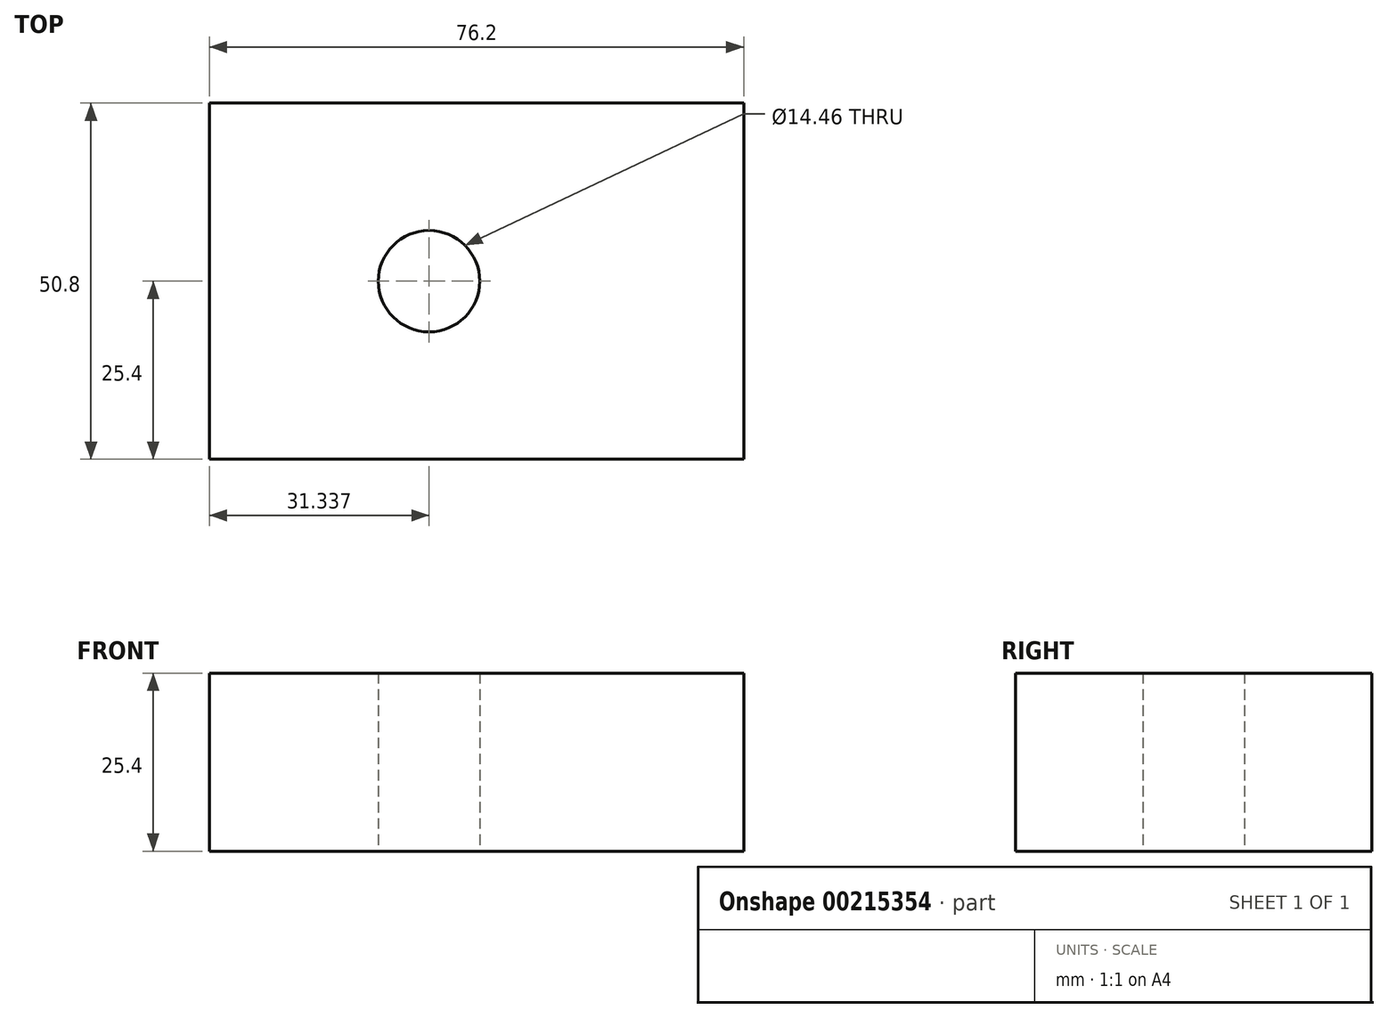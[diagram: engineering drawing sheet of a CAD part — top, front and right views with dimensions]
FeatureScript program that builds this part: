
annotation { "Feature Type Name" : "Feature", "Feature Type Description" : "" }
export const myFeature = defineFeature(function(context is Context, id is Id, definition is map)
    precondition{}
    {
        {
            var Q0;
            Q0=qCreatedBy(makeId("Top.planeOp"),FACE);
            var sketch = newSketch(context, id + "F0", { "sketchPlane" : qUnion([Q0])});
            skLineSegment(sketch, "E0", {"start": v(0, 0) * mm, "end": v(76.2, 0) * mm});
            skLineSegment(sketch, "E1", {"start": v(0, 50.8) * mm, "end": v(0, 0) * mm});
            skLineSegment(sketch, "E2", {"start": v(0, 50.8) * mm, "end": v(76.2, 50.8) * mm});
            skLineSegment(sketch, "E3", {"start": v(76.2, 50.8) * mm, "end": v(76.2, 0) * mm});
            skCircle(sketch, "E4", {"center": v(31.34, 25.4) * mm, "radius": 7.23 * mm});
            skPoint(sketch, "E4.centerSnap0", {"position": v(0, 25.4) * mm});
            skSolve(sketch);
        }
        {
            var Q0;
            Q0=makeQuery(id+"F0.imprint","IMPRINT",FACE,{"disambiguationData":[TD([[makeQuery(id+"F0.imprint","IMPRINT",EDGE,{"derivedFrom":sQuery(id+"F0.wireOp",EDGE,"E0")}),1.0]])]});
            extrude(context, id + "F1", {"entities" : qUnion([Q0]), "depth" : 25.4 * mm});
        }
    });
